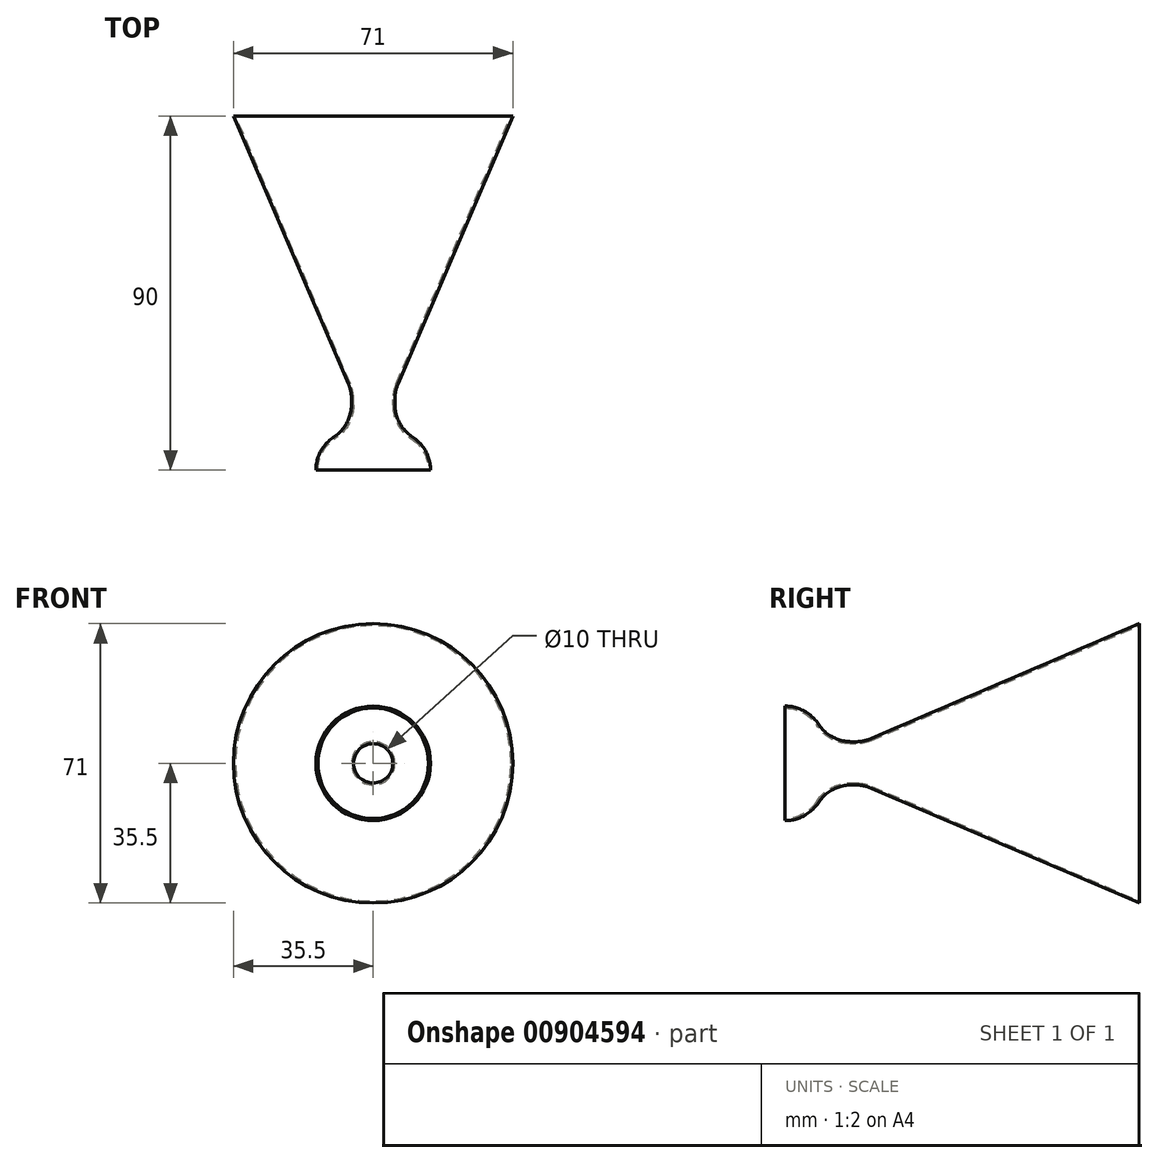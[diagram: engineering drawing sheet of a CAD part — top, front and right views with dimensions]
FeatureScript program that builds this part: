
annotation { "Feature Type Name" : "Feature", "Feature Type Description" : "" }
export const myFeature = defineFeature(function(context is Context, id is Id, definition is map)
    precondition{}
    {
        {
            var Q0;
            Q0=qCreatedBy(makeId("Top.planeOp"),FACE);
            var sketch = newSketch(context, id + "F0", { "sketchPlane" : qUnion([Q0])});
            skLineSegment(sketch, "E0", {"start": v(-5.5, 10) * mm, "end": v(-5.5, 20) * mm});
            skLineSegment(sketch, "E1", {"start": v(-5.5, 20) * mm, "end": v(-35.5, 90) * mm});
            skLineSegment(sketch, "E2", {"start": v(-35.5, 90) * mm, "end": v(-35, 90) * mm});
            skLineSegment(sketch, "E3", {"start": v(-35, 90) * mm, "end": v(-5, 20) * mm});
            skLineSegment(sketch, "E4", {"start": v(-14.05, 0) * mm, "end": v(-14.55, 0) * mm});
            skLineSegment(sketch, "E5", {"start": v(0, 68.6) * mm, "end": v(0, 0) * mm, "construction": true});
            skArc(sketch, "E6", {"start": v(-5.5, 10) * mm, "mid": v(-11.95, 6.74) * mm, "end": v(-14.55, 0) * mm});
            skArc(sketch, "E7", {"start": v(-5, 9.54) * mm, "mid": v(-11.43, 6.57) * mm, "end": v(-14.05, 0) * mm});
            skLineSegment(sketch, "E8", {"start": v(-5, 20) * mm, "end": v(-5, 9.54) * mm});
            skSolve(sketch);
        }
        {
            var Q0;
            Q0=makeQuery(id+"F0.imprint","IMPRINT",FACE,{"disambiguationData":[TD([[makeQuery(id+"F0.imprint","IMPRINT",EDGE,{"derivedFrom":sQuery(id+"F0.wireOp",EDGE,"E0")}),-1.0]])]});
            var Q1;
            Q1=sQuery(id+"F0.wireOp",EDGE,"E5");
            revolve(context, id + "F1", {"surfaceOperationType" : NewSurfaceOperationType.NEW, "entities" : qUnion([Q0]), "axis" : qUnion([Q1]), "revolveType" : RevolveType.FULL});
        }
        {
            var Q0;
            Q0=makeQuery(id+"F1.opRevolve","SWEPT_EDGE",EDGE,{"disambiguationData":[OSD([sQuery(id+"F0.wireOp",EDGE,"E0"),sQuery(id+"F0.wireOp",EDGE,"E6")])]});
            var Q1;
            Q1=makeQuery(id+"F1.opRevolve","SWEPT_EDGE",EDGE,{"disambiguationData":[OSD([sQuery(id+"F0.wireOp",EDGE,"E0"),sQuery(id+"F0.wireOp",EDGE,"E1")])]});
            var Q2;
            Q2=makeQuery(id+"F1.opRevolve","SWEPT_EDGE",EDGE,{"disambiguationData":[OSD([sQuery(id+"F0.wireOp",EDGE,"E7"),sQuery(id+"F0.wireOp",EDGE,"E8")])]});
            var Q3;
            Q3=makeQuery(id+"F1.opRevolve","SWEPT_EDGE",EDGE,{"disambiguationData":[OSD([sQuery(id+"F0.wireOp",EDGE,"E3"),sQuery(id+"F0.wireOp",EDGE,"E8")])]});
            fillet(context, id + "F2", {"entities" : qUnion([Q0, Q1, Q2, Q3]), "radius" : 10 * mm, "tangentPropagation" : true, "allowEdgeOverflow" : false});
        }
    });
